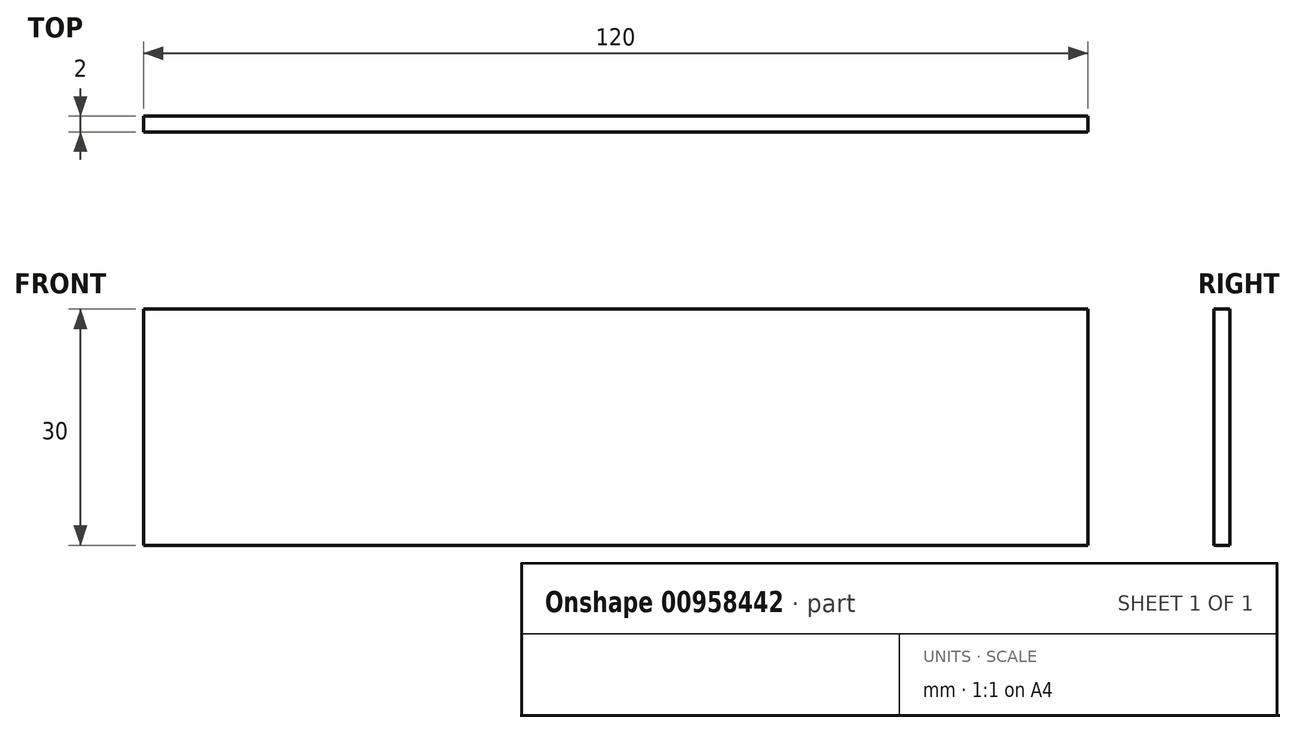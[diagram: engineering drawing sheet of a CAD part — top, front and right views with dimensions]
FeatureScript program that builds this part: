
annotation { "Feature Type Name" : "Feature", "Feature Type Description" : "" }
export const myFeature = defineFeature(function(context is Context, id is Id, definition is map)
    precondition{}
    {
        {
            var Q0;
            Q0=qCreatedBy(makeId("Front.planeOp"),FACE);
            var sketch = newSketch(context, id + "F0", { "sketchPlane" : qUnion([Q0])});
            skLineSegment(sketch, "E0.bottom", {"start": v(60, 15) * mm, "end": v(-60, 15) * mm});
            skLineSegment(sketch, "E0.top", {"start": v(60, -15) * mm, "end": v(-60, -15) * mm});
            skLineSegment(sketch, "E0.left", {"start": v(60, 15) * mm, "end": v(60, -15) * mm});
            skLineSegment(sketch, "E0.right", {"start": v(-60, 15) * mm, "end": v(-60, -15) * mm});
            skPoint(sketch, "E0.middle", {"position": v(0, 0) * mm});
            skSolve(sketch);
        }
        {
            var Q0;
            Q0=makeQuery(id+"F0.imprint","IMPRINT",FACE,{"disambiguationData":[TD([[makeQuery(id+"F0.imprint","IMPRINT",EDGE,{"derivedFrom":sQuery(id+"F0.wireOp",EDGE,"E0.bottom")}),1.0]])]});
            extrude(context, id + "F1", {"entities" : qUnion([Q0]), "depth" : 2 * mm, "offsetDistance" : 25 * mm});
        }
    });
